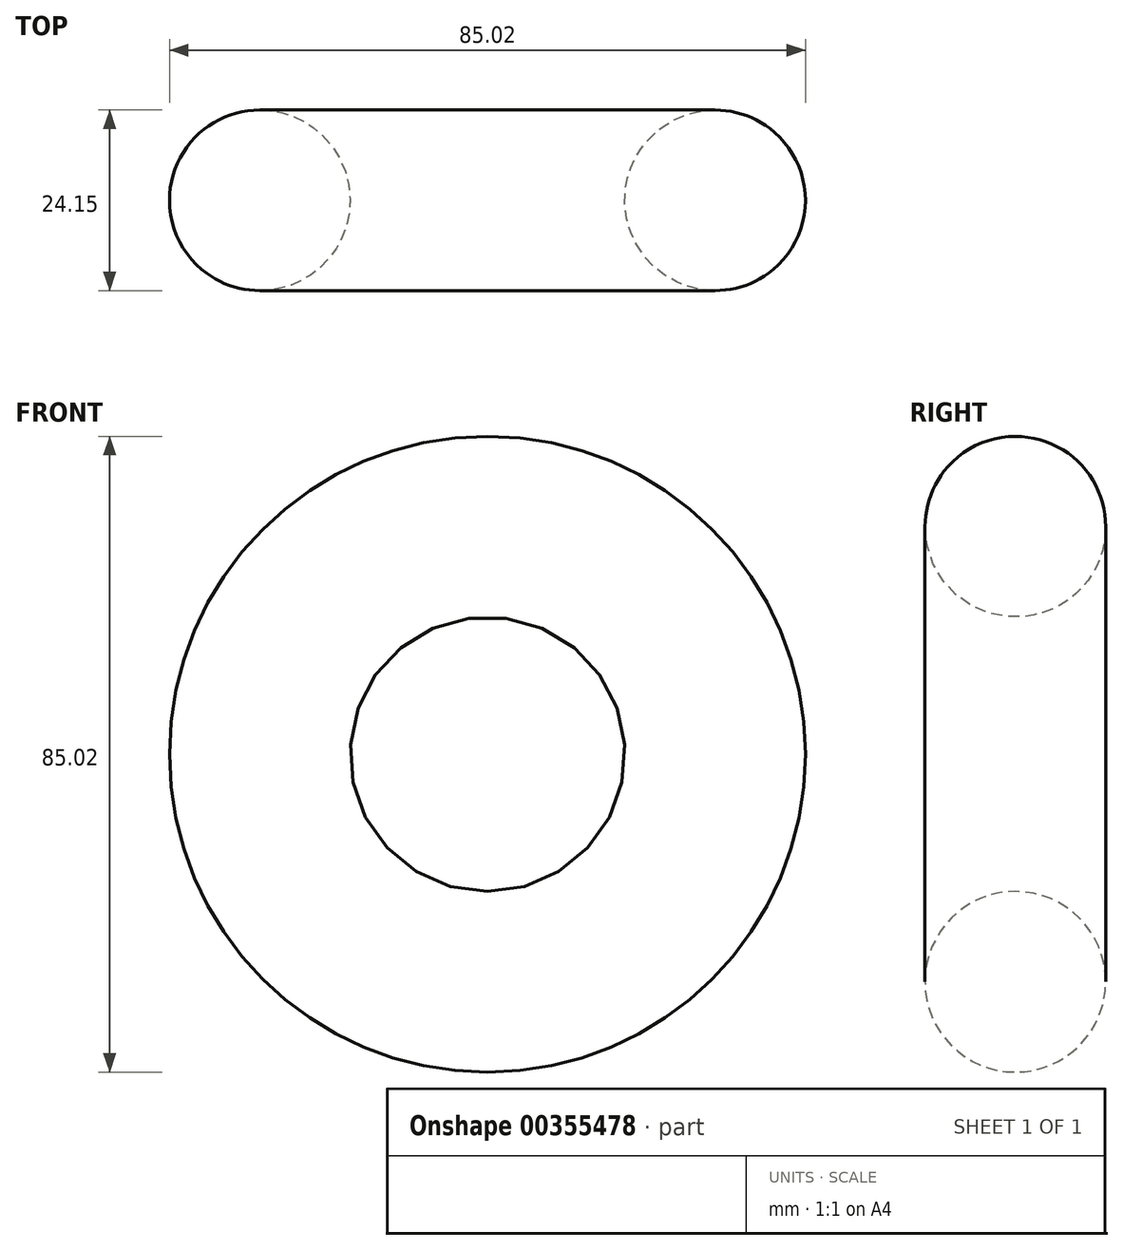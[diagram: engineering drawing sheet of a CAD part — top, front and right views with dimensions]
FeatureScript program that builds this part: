
annotation { "Feature Type Name" : "Feature", "Feature Type Description" : "" }
export const myFeature = defineFeature(function(context is Context, id is Id, definition is map)
    precondition{}
    {
        {
            var Q0;
            Q0=qCreatedBy(makeId("Front.planeOp"),FACE);
            var sketch = newSketch(context, id + "F0", { "sketchPlane" : qUnion([Q0])});
            skCircle(sketch, "E0", {"center": v(-41.18, 45.25) * mm, "radius": 19.48 * mm});
            skSolve(sketch);
        }
        {
            var Q0;
            Q0=qCreatedBy(makeId("Top.planeOp"),FACE);
            var sketch = newSketch(context, id + "F1", { "sketchPlane" : qUnion([Q0])});
            skLineSegment(sketch, "E1", {"start": v(-14, -41.7) * mm, "end": v(-54.79, -41.7) * mm});
            skSolve(sketch);
        }
        {
            var Q0;
            Q0=sQuery(id+"F0.wireOp",EDGE,"E0");
            var Q1;
            Q1=sQuery(id+"F1.wireOp",EDGE,"E1");
            revolve(context, id + "F2", {"bodyType" : ToolBodyType.SURFACE, "surfaceEntities" : qUnion([Q0]), "axis" : qUnion([Q1]), "revolveType" : RevolveType.FULL});
        }
        {
            var Q0;
            Q0=qCreatedBy(makeId("Right.planeOp"),FACE);
            var sketch = newSketch(context, id + "F3", { "sketchPlane" : qUnion([Q0])});
            skCircle(sketch, "E2", {"center": v(-38.64, 6.73) * mm, "radius": 12.08 * mm});
            skLineSegment(sketch, "E3", {"start": v(-54.28, 37.16) * mm, "end": v(-23, 37.16) * mm});
            skSolve(sketch);
        }
        {
            var Q0;
            Q0=makeQuery(id+"F3.imprint","IMPRINT",FACE,{"disambiguationData":[TD([[makeQuery(id+"F3.imprint","IMPRINT",EDGE,{"derivedFrom":sQuery(id+"F3.wireOp",EDGE,"E2")}),1.0]])]});
            var Q1;
            Q1=sQuery(id+"F3.wireOp",EDGE,"E3");
            revolve(context, id + "F4", {"entities" : qUnion([Q0]), "axis" : qUnion([Q1]), "revolveType" : RevolveType.FULL});
        }
    });
